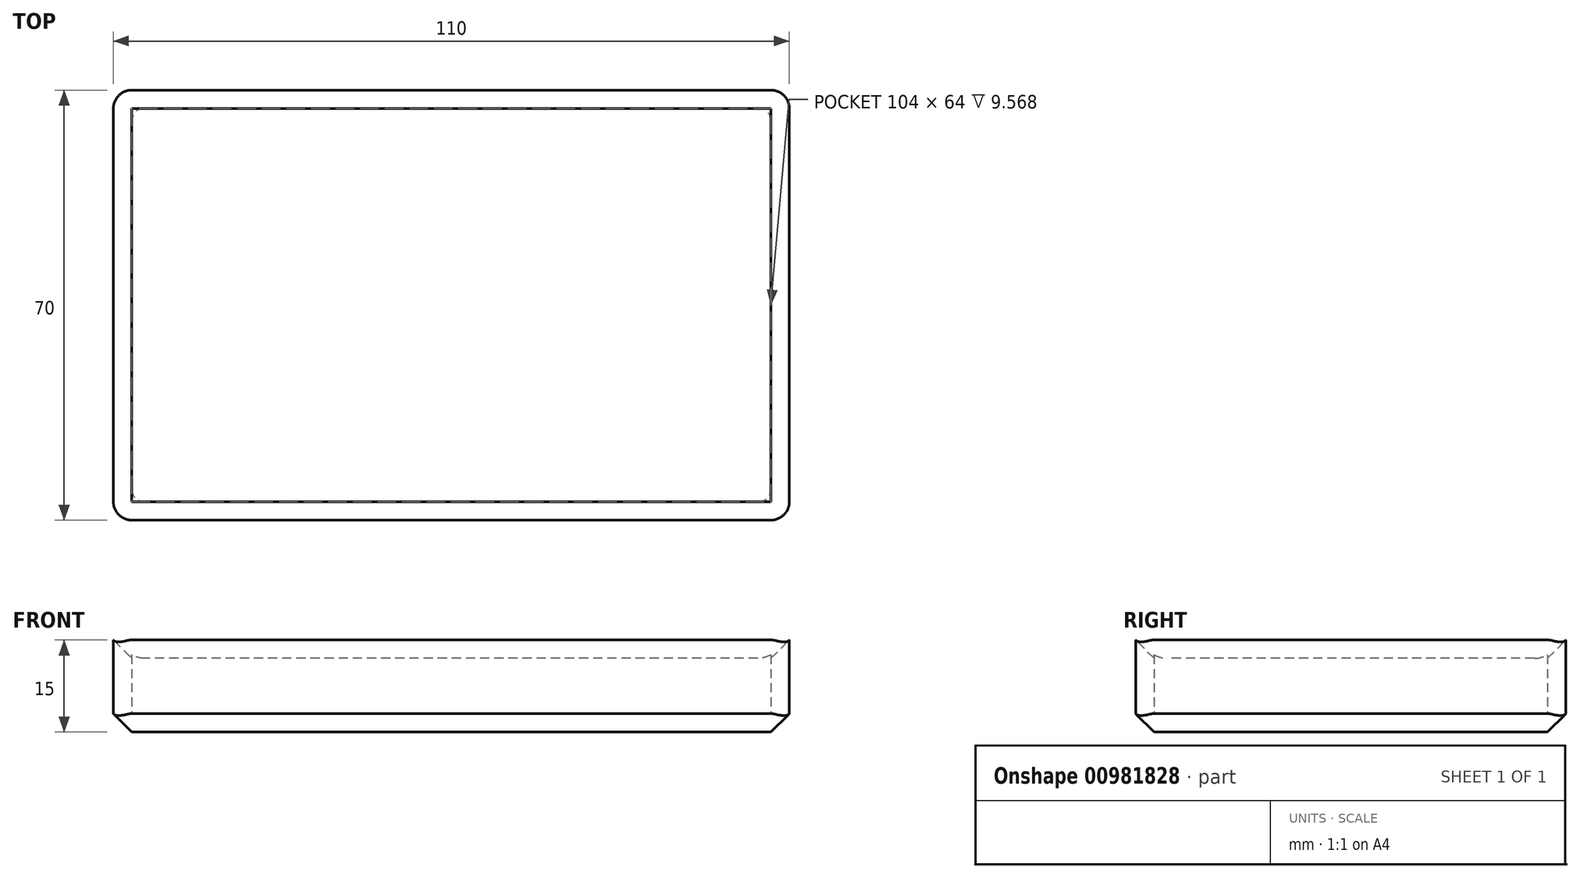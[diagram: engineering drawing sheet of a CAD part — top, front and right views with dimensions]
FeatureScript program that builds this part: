
annotation { "Feature Type Name" : "Feature", "Feature Type Description" : "" }
export const myFeature = defineFeature(function(context is Context, id is Id, definition is map)
    precondition{}
    {
        {
            var Q0;
            Q0=qCreatedBy(makeId("Top.planeOp"),FACE);
            var sketch = newSketch(context, id + "F0", { "sketchPlane" : qUnion([Q0])});
            skLineSegment(sketch, "E0.bottom", {"start": v(-42.8, 28.8) * mm, "end": v(67.2, 28.8) * mm});
            skLineSegment(sketch, "E0.top", {"start": v(-42.8, -41.2) * mm, "end": v(67.2, -41.2) * mm});
            skLineSegment(sketch, "E0.left", {"start": v(-42.8, 28.8) * mm, "end": v(-42.8, -41.2) * mm});
            skLineSegment(sketch, "E0.right", {"start": v(67.2, 28.8) * mm, "end": v(67.2, -41.2) * mm});
            skSolve(sketch);
        }
        {
            var Q0;
            Q0=makeQuery(id+"F0.imprint","IMPRINT",FACE,{"disambiguationData":[TD([[makeQuery(id+"F0.imprint","IMPRINT",EDGE,{"derivedFrom":sQuery(id+"F0.wireOp",EDGE,"E0.bottom")}),-1.0]])]});
            extrude(context, id + "F1", {"entities" : qUnion([Q0]), "depth" : 15 * mm, "offsetDistance" : 25 * mm});
        }
        {
            var Q0;
            Q0=makeQuery(id+"F1.opExtrude","CAP_FACE",FACE,{"disambiguationData":[OSD([sQuery(id+"F0.wireOp",EDGE,"E0.bottom"),sQuery(id+"F0.wireOp",EDGE,"E0.top"),sQuery(id+"F0.wireOp",EDGE,"E0.left"),sQuery(id+"F0.wireOp",EDGE,"E0.right")])],"isStart":false});
            shell(context, id + "F2", {"entities" : qUnion([Q0]), "thickness" : 3 * mm});
        }
        {
            var Q0;
            Q0=makeQuery(id+"F1.opExtrude","CAP_EDGE",EDGE,{"disambiguationData":[OSD([sQuery(id+"F0.wireOp",EDGE,"E0.left")])],"isStart":true});
            var Q1;
            Q1=makeQuery(id+"F1.opExtrude","CAP_EDGE",EDGE,{"disambiguationData":[OSD([sQuery(id+"F0.wireOp",EDGE,"E0.top")])],"isStart":true});
            var Q2;
            Q2=makeQuery(id+"F1.opExtrude","CAP_EDGE",EDGE,{"disambiguationData":[OSD([sQuery(id+"F0.wireOp",EDGE,"E0.right")])],"isStart":true});
            var Q3;
            Q3=makeQuery(id+"F1.opExtrude","CAP_EDGE",EDGE,{"disambiguationData":[OSD([sQuery(id+"F0.wireOp",EDGE,"E0.bottom")])],"isStart":true});
            chamfer(context, id + "F3", {"entities" : qUnion([Q0, Q1, Q2, Q3]), "width" : 3 * mm, "tangentPropagation" : true});
        }
        {
            var Q0;
            {var subQ0=sQuery(id+"F0.wireOp",EDGE,"E0.bottom");Q0=makeQuery(id+"F2.opShell","OFFSET_EDGE",EDGE,{"disambiguationData":[OSD([subQ0]),TDD([makeQuery(id+"F1.opExtrude","CAP_EDGE",EDGE,{"disambiguationData":[OSD([subQ0])],"isStart":false})])]});}
            var Q1;
            {var subQ0=sQuery(id+"F0.wireOp",EDGE,"E0.left");Q1=makeQuery(id+"F2.opShell","OFFSET_EDGE",EDGE,{"disambiguationData":[OSD([subQ0]),TDD([makeQuery(id+"F1.opExtrude","CAP_EDGE",EDGE,{"disambiguationData":[OSD([subQ0])],"isStart":false})])]});}
            var Q2;
            {var subQ0=sQuery(id+"F0.wireOp",EDGE,"E0.right");Q2=makeQuery(id+"F2.opShell","OFFSET_EDGE",EDGE,{"disambiguationData":[OSD([subQ0]),TDD([makeQuery(id+"F1.opExtrude","CAP_EDGE",EDGE,{"disambiguationData":[OSD([subQ0])],"isStart":false})])]});}
            var Q3;
            {var subQ0=sQuery(id+"F0.wireOp",EDGE,"E0.top");Q3=makeQuery(id+"F2.opShell","OFFSET_EDGE",EDGE,{"disambiguationData":[OSD([subQ0]),TDD([makeQuery(id+"F1.opExtrude","CAP_EDGE",EDGE,{"disambiguationData":[OSD([subQ0])],"isStart":false})])]});}
            chamfer(context, id + "F4", {"entities" : qUnion([Q0, Q1, Q2, Q3]), "width" : 3 * mm, "tangentPropagation" : true});
        }
        {
            var Q0;
            Q0=makeQuery(id+"F1.opExtrude","SWEPT_EDGE",EDGE,{"disambiguationData":[OSD([sQuery(id+"F0.wireOp",EDGE,"E0.top"),sQuery(id+"F0.wireOp",EDGE,"E0.right")])]});
            var Q1;
            Q1=makeQuery(id+"F1.opExtrude","SWEPT_EDGE",EDGE,{"disambiguationData":[OSD([sQuery(id+"F0.wireOp",EDGE,"E0.top"),sQuery(id+"F0.wireOp",EDGE,"E0.left")])]});
            var Q2;
            Q2=makeQuery(id+"F1.opExtrude","SWEPT_EDGE",EDGE,{"disambiguationData":[OSD([sQuery(id+"F0.wireOp",EDGE,"E0.bottom"),sQuery(id+"F0.wireOp",EDGE,"E0.right")])]});
            var Q3;
            Q3=makeQuery(id+"F1.opExtrude","SWEPT_EDGE",EDGE,{"disambiguationData":[OSD([sQuery(id+"F0.wireOp",EDGE,"E0.bottom"),sQuery(id+"F0.wireOp",EDGE,"E0.left")])]});
            var Q4;
            {var subQ0=sQuery(id+"F0.wireOp",EDGE,"E0.right");var subQ1=sQuery(id+"F0.wireOp",EDGE,"E0.top");Q4=makeQuery(id+"F4.opChamfer","BLEND_EDGE",EDGE,{"blendedFrom":[makeQuery(id+"F2.opShell","OFFSET_EDGE",EDGE,{"disambiguationData":[OSD([subQ1]),TDD([makeQuery(id+"F1.opExtrude","CAP_EDGE",EDGE,{"disambiguationData":[OSD([subQ1])],"isStart":false})])]}),makeQuery(id+"F2.opShell","OFFSET_EDGE",EDGE,{"disambiguationData":[OSD([subQ0]),TDD([makeQuery(id+"F1.opExtrude","CAP_EDGE",EDGE,{"disambiguationData":[OSD([subQ0])],"isStart":false})])]})],"blendedInto":[]});}
            var Q5;
            {var subQ0=sQuery(id+"F0.wireOp",EDGE,"E0.left");var subQ1=sQuery(id+"F0.wireOp",EDGE,"E0.top");Q5=makeQuery(id+"F4.opChamfer","BLEND_EDGE",EDGE,{"blendedFrom":[makeQuery(id+"F2.opShell","OFFSET_EDGE",EDGE,{"disambiguationData":[OSD([subQ1]),TDD([makeQuery(id+"F1.opExtrude","CAP_EDGE",EDGE,{"disambiguationData":[OSD([subQ1])],"isStart":false})])]}),makeQuery(id+"F2.opShell","OFFSET_EDGE",EDGE,{"disambiguationData":[OSD([subQ0]),TDD([makeQuery(id+"F1.opExtrude","CAP_EDGE",EDGE,{"disambiguationData":[OSD([subQ0])],"isStart":false})])]})],"blendedInto":[]});}
            var Q6;
            {var subQ0=sQuery(id+"F0.wireOp",EDGE,"E0.left");var subQ1=sQuery(id+"F0.wireOp",EDGE,"E0.bottom");Q6=makeQuery(id+"F4.opChamfer","BLEND_EDGE",EDGE,{"blendedFrom":[makeQuery(id+"F2.opShell","OFFSET_EDGE",EDGE,{"disambiguationData":[OSD([subQ1]),TDD([makeQuery(id+"F1.opExtrude","CAP_EDGE",EDGE,{"disambiguationData":[OSD([subQ1])],"isStart":false})])]}),makeQuery(id+"F2.opShell","OFFSET_EDGE",EDGE,{"disambiguationData":[OSD([subQ0]),TDD([makeQuery(id+"F1.opExtrude","CAP_EDGE",EDGE,{"disambiguationData":[OSD([subQ0])],"isStart":false})])]})],"blendedInto":[]});}
            var Q7;
            {var subQ0=sQuery(id+"F0.wireOp",EDGE,"E0.right");var subQ1=sQuery(id+"F0.wireOp",EDGE,"E0.bottom");Q7=makeQuery(id+"F4.opChamfer","BLEND_EDGE",EDGE,{"blendedFrom":[makeQuery(id+"F2.opShell","OFFSET_EDGE",EDGE,{"disambiguationData":[OSD([subQ1]),TDD([makeQuery(id+"F1.opExtrude","CAP_EDGE",EDGE,{"disambiguationData":[OSD([subQ1])],"isStart":false})])]}),makeQuery(id+"F2.opShell","OFFSET_EDGE",EDGE,{"disambiguationData":[OSD([subQ0]),TDD([makeQuery(id+"F1.opExtrude","CAP_EDGE",EDGE,{"disambiguationData":[OSD([subQ0])],"isStart":false})])]})],"blendedInto":[]});}
            var Q8;
            Q8=makeQuery(id+"F3.opChamfer","BLEND_EDGE",EDGE,{"blendedFrom":[makeQuery(id+"F1.opExtrude","CAP_EDGE",EDGE,{"disambiguationData":[OSD([sQuery(id+"F0.wireOp",EDGE,"E0.top")])],"isStart":true}),makeQuery(id+"F1.opExtrude","CAP_EDGE",EDGE,{"disambiguationData":[OSD([sQuery(id+"F0.wireOp",EDGE,"E0.left")])],"isStart":true})],"blendedInto":[]});
            var Q9;
            Q9=makeQuery(id+"F3.opChamfer","BLEND_EDGE",EDGE,{"blendedFrom":[makeQuery(id+"F1.opExtrude","CAP_EDGE",EDGE,{"disambiguationData":[OSD([sQuery(id+"F0.wireOp",EDGE,"E0.bottom")])],"isStart":true}),makeQuery(id+"F1.opExtrude","CAP_EDGE",EDGE,{"disambiguationData":[OSD([sQuery(id+"F0.wireOp",EDGE,"E0.left")])],"isStart":true})],"blendedInto":[]});
            var Q10;
            Q10=makeQuery(id+"F3.opChamfer","BLEND_EDGE",EDGE,{"blendedFrom":[makeQuery(id+"F1.opExtrude","CAP_EDGE",EDGE,{"disambiguationData":[OSD([sQuery(id+"F0.wireOp",EDGE,"E0.top")])],"isStart":true}),makeQuery(id+"F1.opExtrude","CAP_EDGE",EDGE,{"disambiguationData":[OSD([sQuery(id+"F0.wireOp",EDGE,"E0.right")])],"isStart":true})],"blendedInto":[]});
            var Q11;
            Q11=makeQuery(id+"F3.opChamfer","BLEND_EDGE",EDGE,{"blendedFrom":[makeQuery(id+"F1.opExtrude","CAP_EDGE",EDGE,{"disambiguationData":[OSD([sQuery(id+"F0.wireOp",EDGE,"E0.bottom")])],"isStart":true}),makeQuery(id+"F1.opExtrude","CAP_EDGE",EDGE,{"disambiguationData":[OSD([sQuery(id+"F0.wireOp",EDGE,"E0.right")])],"isStart":true})],"blendedInto":[]});
            fillet(context, id + "F5", {"entities" : qUnion([Q0, Q1, Q2, Q3, Q4, Q5, Q6, Q7, Q8, Q9, Q10, Q11]), "radius" : 3 * mm, "tangentPropagation" : true, "allowEdgeOverflow" : false});
        }
    });
